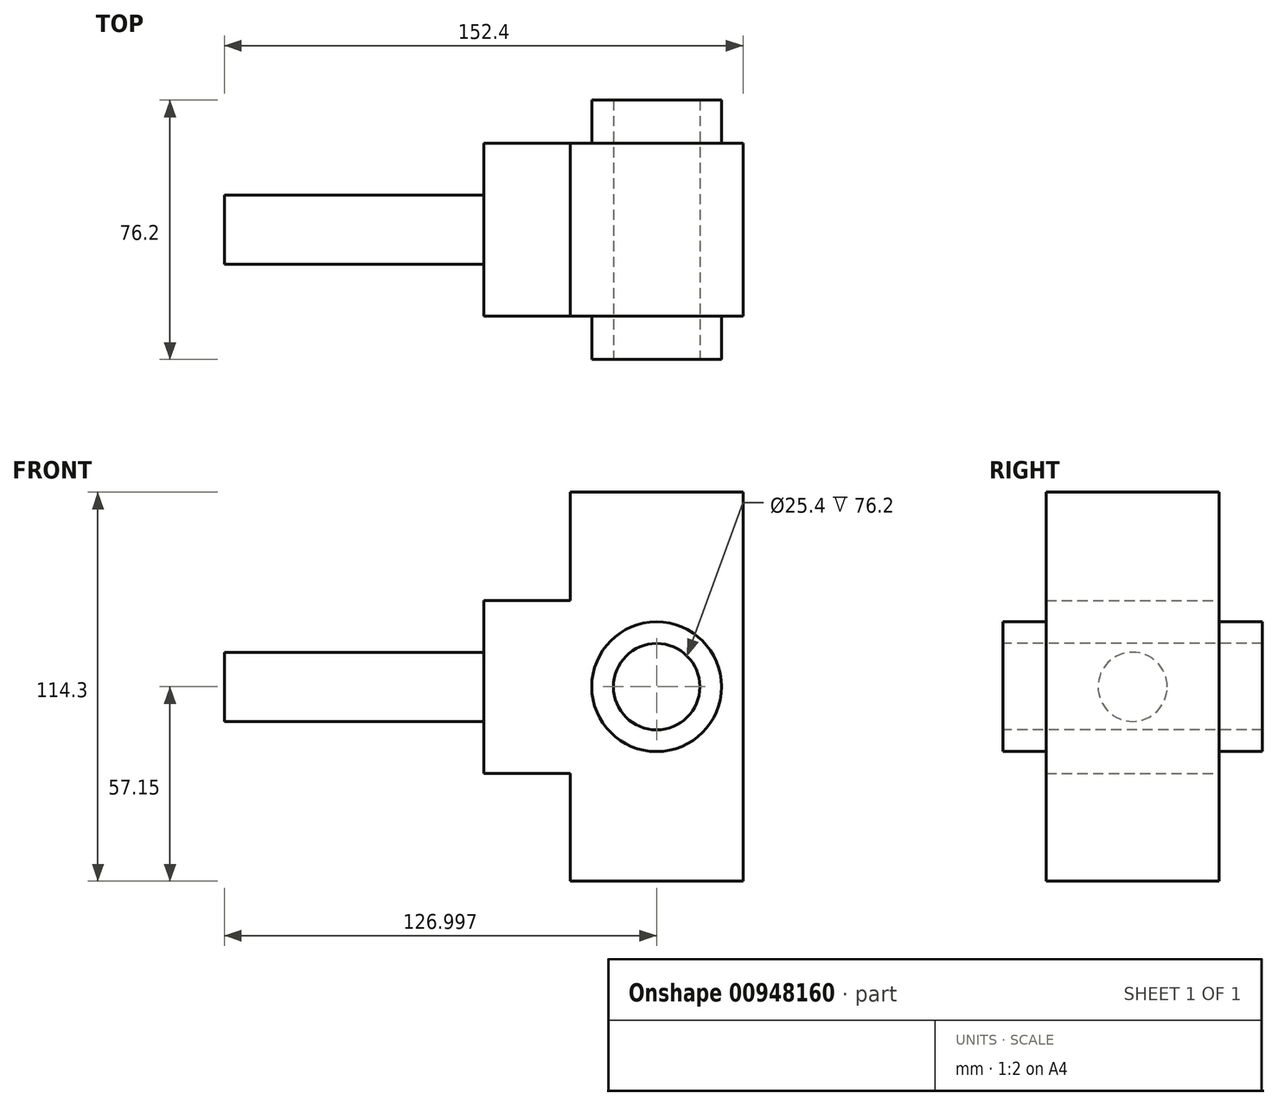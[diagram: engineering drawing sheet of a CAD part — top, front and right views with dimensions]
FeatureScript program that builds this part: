
annotation { "Feature Type Name" : "Feature", "Feature Type Description" : "" }
export const myFeature = defineFeature(function(context is Context, id is Id, definition is map)
    precondition{}
    {
        {
            var Q0;
            Q0=qCreatedBy(makeId("Top.planeOp"),FACE);
            var sketch = newSketch(context, id + "F0", { "sketchPlane" : qUnion([Q0])});
            skLineSegment(sketch, "E0.bottom", {"start": v(-49.77, 25.17) * mm, "end": v(1.03, 25.17) * mm});
            skLineSegment(sketch, "E0.top", {"start": v(-49.77, -25.63) * mm, "end": v(1.03, -25.63) * mm});
            skLineSegment(sketch, "E0.left", {"start": v(-49.77, 25.17) * mm, "end": v(-49.77, -25.63) * mm});
            skLineSegment(sketch, "E0.right", {"start": v(1.03, 25.17) * mm, "end": v(1.03, -25.63) * mm});
            skSolve(sketch);
        }
        {
            var Q0;
            Q0=makeQuery(id+"F0.imprint","IMPRINT",FACE,{"disambiguationData":[TD([[makeQuery(id+"F0.imprint","IMPRINT",EDGE,{"derivedFrom":sQuery(id+"F0.wireOp",EDGE,"E0.bottom")}),-1.0]])]});
            extrude(context, id + "F1", {"entities" : qUnion([Q0]), "depth" : 114.3 * mm, "offsetDistance" : 25.4 * mm});
        }
        {
            var Q0;
            Q0=makeQuery(id+"F1.opExtrude","SWEPT_FACE",FACE,{"disambiguationData":[OSD([sQuery(id+"F0.wireOp",EDGE,"E0.top")])]});
            var sketch = newSketch(context, id + "F2", { "sketchPlane" : qUnion([Q0])});
            skCircle(sketch, "E1", {"center": v(-24.37, 57.15) * mm, "radius": 12.7 * mm});
            skPoint(sketch, "E1.centerSnap0", {"position": v(-24.37, 114.3) * mm});
            skCircle(sketch, "E2", {"center": v(-24.37, 57.15) * mm, "radius": 19.05 * mm});
            skSolve(sketch);
        }
        {
            var Q0;
            Q0=makeQuery(id+"F2.imprint","IMPRINT",FACE,{"disambiguationData":[TD([[makeQuery(id+"F2.imprint","IMPRINT",EDGE,{"derivedFrom":sQuery(id+"F2.wireOp",EDGE,"E1")}),1.0]])]});
            extrude(context, id + "F3", {"entities" : qUnion([Q0]), "operationType" : NewBodyOperationType.REMOVE, "oppositeDirection" : true, "depth" : 76.2 * mm, "offsetDistance" : 25.4 * mm});
        }
        {
            var Q0;
            Q0=makeQuery(id+"F2.imprint","IMPRINT",FACE,{"disambiguationData":[TD([[makeQuery(id+"F2.imprint","IMPRINT",EDGE,{"derivedFrom":sQuery(id+"F2.wireOp",EDGE,"E1")}),-1.0]])]});
            extrude(context, id + "F4", {"entities" : qUnion([Q0]), "operationType" : NewBodyOperationType.ADD, "depth" : 12.7 * mm, "offsetDistance" : 25.4 * mm, "hasSecondDirection" : true, "secondDirectionOppositeDirection" : true, "secondDirectionDepth" : 63.5 * mm});
        }
        {
            var Q0;
            Q0=makeQuery(id+"F1.opExtrude","SWEPT_FACE",FACE,{"disambiguationData":[OSD([sQuery(id+"F0.wireOp",EDGE,"E0.left")])]});
            var sketch = newSketch(context, id + "F5", { "sketchPlane" : qUnion([Q0])});
            skCircle(sketch, "E3", {"center": v(0.23, 57.13) * mm, "radius": 10.16 * mm});
            skPoint(sketch, "E3.centerSnap0", {"position": v(0.23, 114.3) * mm});
            skLineSegment(sketch, "E4.bottom", {"start": v(25.63, 82.53) * mm, "end": v(-25.17, 82.53) * mm});
            skLineSegment(sketch, "E4.top", {"start": v(25.63, 31.73) * mm, "end": v(-25.17, 31.73) * mm});
            skLineSegment(sketch, "E4.left", {"start": v(25.63, 82.53) * mm, "end": v(25.63, 31.73) * mm});
            skLineSegment(sketch, "E4.right", {"start": v(-25.17, 82.53) * mm, "end": v(-25.17, 31.73) * mm});
            skSolve(sketch);
        }
        {
            var Q0;
            Q0=makeQuery(id+"F5.imprint","IMPRINT",FACE,{"disambiguationData":[TD([[makeQuery(id+"F5.imprint","IMPRINT",EDGE,{"derivedFrom":sQuery(id+"F5.wireOp",EDGE,"E3")}),1.0]])]});
            extrude(context, id + "F6", {"entities" : qUnion([Q0]), "operationType" : NewBodyOperationType.ADD, "depth" : 101.6 * mm, "offsetDistance" : 25.4 * mm});
        }
        {
            var Q0;
            Q0=makeQuery(id+"F5.imprint","IMPRINT",FACE,{"disambiguationData":[TD([[makeQuery(id+"F5.imprint","IMPRINT",EDGE,{"derivedFrom":sQuery(id+"F5.wireOp",EDGE,"E3")}),-1.0]])]});
            extrude(context, id + "F7", {"entities" : qUnion([Q0]), "operationType" : NewBodyOperationType.ADD, "depth" : 25.4 * mm, "offsetDistance" : 25.4 * mm});
        }
    });
